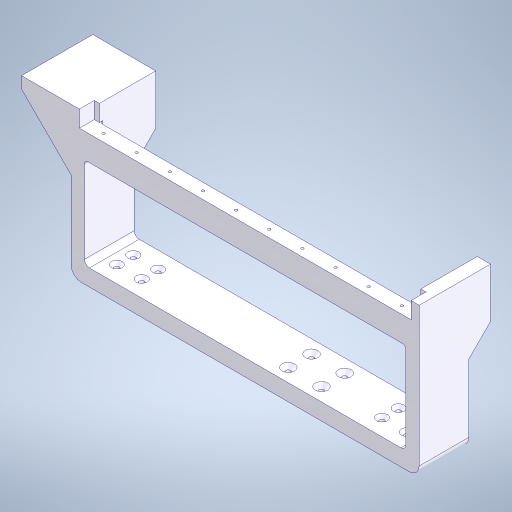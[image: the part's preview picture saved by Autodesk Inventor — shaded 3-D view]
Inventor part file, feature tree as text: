
AUTODESK INVENTOR PART (.ipt)
format: ipt  version: 2024 (Build 280153000, 153)  size: 425,472 bytes
history: native  units: in
note: dims shown in document units (in); Inventor stores cm internally (conversion verified against a paired STEP export)
features: extrude x10, sketch x10, chamfer x4, fillet x3
ambient origin geometry x8: Origin, YZ Plane, XZ Plane, XY Plane, X Axis, Y Axis, Z Axis, Center Point
bodies: Solid1 (feature_tree)
feature tree (27):
  extrude  "Extrusion1"  Depth=3.5433in
  extrude  "Extrusion2"  Depth=0.315in
  extrude  "Extrusion3"  Depth=0.3937in
  chamfer  "Chamfer1"  Distance=1.1811in
  extrude  "Extrusion9"  Depth=0.1181in
  chamfer  "Chamfer4"  Distance=0.3937in
  extrude  "Extrusion12"  Depth=0.3937in
  fillet  "Fillet3"  Radius=0.3937in
  extrude  "Extrusion14"  Depth=0.3937in
  extrude  "Extrusion15"  Depth=0.5906in
  fillet  "Fillet4"  Radius=0.5906in
  fillet  "Fillet5"  Radius=0.374in
  extrude  "Extrusion17"  Depth=0.5906in
  chamfer  "Chamfer10"  Distance=0.5906in
  extrude  "Extrusion19"  Depth=0.0787in
  extrude  "Extrusion20"  Depth=0.3937in
  chamfer  "Chamfer12"  Distance=0.3937in
  sketch  "Sketch1"  dims[d0=8.2677in d1=3.5433in]
  sketch  "Sketch2"  dims[d2=1.1811in d3=0.0in d4=0.315in]
  sketch  "Sketch3"  dims[d5=0.315in d6=0.3937in d7=1.1811in d8=0.0in]
  sketch  "Sketch9"  dims[d9=0.1181in d10=0.1181in]
  sketch  "Sketch12"  dims[d11=0.1181in]
  sketch  "Sketch14"  dims[d12=0.1181in]
  sketch  "Sketch15"  dims[d13=0.1181in]
  sketch  "Sketch17"  dims[d14=0.1181in]
  sketch  "Sketch19"  dims[d15=0.1181in]
  sketch  "Sketch20"  dims[d16=0.1181in d18=0.3937in d19=0.3937in d20=0.3937in d21=0.3937in d22=0.5906in d23=0.5906in d24=0.374in d25=0.5906in d26=0.5906in d27=0.374in d28=0.3937in d29=0.3937in d30=0.3937in d31=0.3937in d33=5.7087in d34=5.7087in d35=1.1811in d36=0.0in d37=0.0709in d38=0.125in d39=45.0deg d74=1.1811in d75=1.1811in d76=0.5118in d77=0.0in d78=0.5118in d79=0.0787in d80=45.0deg d90=0.315in d97=0.3543in d98=0.5906in d99=0.3937in d100=7.6378in d101=0.0in d107=0.0787in d108=0.3543in d109=0.122in d110=0.122in d111=0.3937in d112=0.0in d116=0.3976in d117=0.1772in d118=3.937in d120=0.7874in d121=0.3937in d123=0.3937in d125=0.5906in d126=0.0in d127=0.063in d152=0.1181in d153=0.2362in d155=0.1181in d156=0.1181in d157=0.1181in d158=0.1181in d159=0.315in d160=0.315in d161=0.315in d162=0.315in d163=0.7874in d164=0.7874in d165=4.5276in d166=4.5276in d167=0.3937in d168=0.0in d169=0.0906in d170=0.0787in d171=45.0deg d178=0.2756in d179=1.1811in d180=0.0in d181=0.2756in d182=1.1811in d183=1.1811in d184=0.0in d185=1.1811in d186=0.0787in d187=45.0deg]
